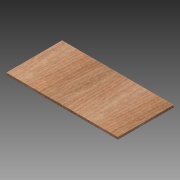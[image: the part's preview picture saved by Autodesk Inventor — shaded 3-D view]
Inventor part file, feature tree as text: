
AUTODESK INVENTOR PART (.ipt)
format: ipt  version: 2015 SP1 (Build 190203100, 203)  size: 88,576 bytes
history: native  units: mm
features: extrude x1, sketch x1
ambient origin geometry x8: Origin, YZ Plane, XZ Plane, XY Plane, X Axis, Y Axis, Z Axis, Center Point
bodies: Solid1 (feature_tree)
feature tree (2):
  extrude  "Extrusion1"  Depth=200.0mm
  sketch  "Sketch1"  dims[d0=400.0mm d1=200.0mm d2=8.0mm d3=0.0mm]
